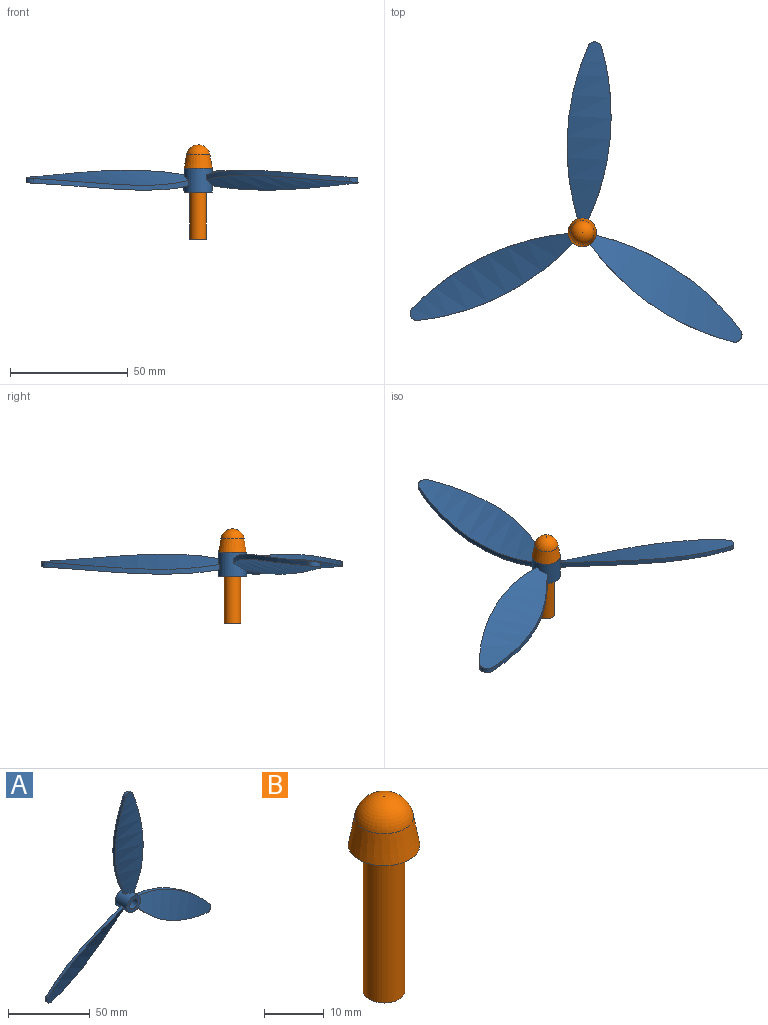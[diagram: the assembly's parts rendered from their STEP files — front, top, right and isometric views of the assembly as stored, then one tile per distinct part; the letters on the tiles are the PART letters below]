
ASSEMBLY  parts=2 mates=1
PART A: 19 faces, bbox 188.2x16.7x163 mm
  f0: bspline ~100x30mm, area 1083.3mm2, adj f1,f2,f4,f15
  f1: cylinder r=106mm len=73.47mm, axis (0,1,0), area 154.2mm2, adj f0,f3,f4,f15
  f2: cylinder r=106mm len=73.47mm, axis (0,1,0), area 154.2mm2, adj f0,f3,f4,f15
  f3: bspline ~100x30mm, area 1083.3mm2, adj f1,f2,f4,f15
  f4: cylinder r=3mm len=5.64mm, axis (0,1,0), area 14.4mm2, adj f0,f1,f2,f3
  f5: bspline ~100.35x74.67mm, area 1083.3mm2, adj f6,f7,f9,f15
  f6: cylinder r=106mm len=63.35mm, axis (0,1,0), area 154.2mm2, adj f5,f8,f9,f15
  f7: cylinder r=106mm len=63.9mm, axis (0,1,0), area 154.2mm2, adj f5,f8,f9,f15
  f8: bspline ~100.85x73.81mm, area 1083.3mm2, adj f6,f7,f9,f15
  f9: cylinder r=3mm len=4.93mm, axis (0,1,0), area 14.4mm2, adj f5,f6,f7,f8
  f10: bspline ~100.85x73.81mm, area 1083.3mm2, adj f11,f12,f14,f15
  f11: cylinder r=106mm len=63.9mm, axis (0,1,0), area 154.2mm2, adj f10,f13,f14,f15
  f12: cylinder r=106mm len=63.35mm, axis (0,1,0), area 154.2mm2, adj f10,f13,f14,f15
  f13: bspline ~100.35x74.67mm, area 1083.3mm2, adj f11,f12,f14,f15
  f14: cylinder r=3mm len=4.93mm, axis (0,1,0), area 14.4mm2, adj f10,f11,f12,f13
  f15: cylinder r=6mm len=12mm, axis (0,1,0), area 345.3mm2, adj f0,f1,f2,f3,f5,f6,f7,f8
  f16: plane 12x12mm, normal (0,-1,0), area 74.6mm2, adj f15,f18
  f17: plane 12x12mm, normal (0,1,0), area 74.6mm2, adj f15,f18
  f18: cylinder r=3.5mm len=10mm, axis (0,-1,0), area 219.9mm2, adj f16,f17
PART B: 6 faces, bbox 12x12x40 mm
  f0: cylinder r=3.5mm len=30mm, axis (0,0,-1), area 659.7mm2, adj f1,f4
  f1: plane 7x7mm, normal (0,0,-1), area 38.5mm2, adj f0
  f2: cone r=6mm half-angle=10deg, axis (0,0,-1), area 205.3mm2, adj f4,f5
  f3: plane 0.08x0.08mm, normal (0,0,1), area 0mm2, adj f5
  f4: plane 12x12mm, normal (0,0,-1), area 74.6mm2, adj f0,f2
  f5: torus R=0.04mm, axis (0,0,1), area 131.6mm2, adj f2,f3
PLACE A rot(axis=(-0.35,0.66,-0.66),141.1deg) t=(-43.38,14.07,63.02)mm
PLACE B t=(-43.38,14.07,38.02)mm fixed
MATE revolute B.f2 <-> A.f18  axis (0,0,-1) through (-43.38,14.07,68.02)mm
